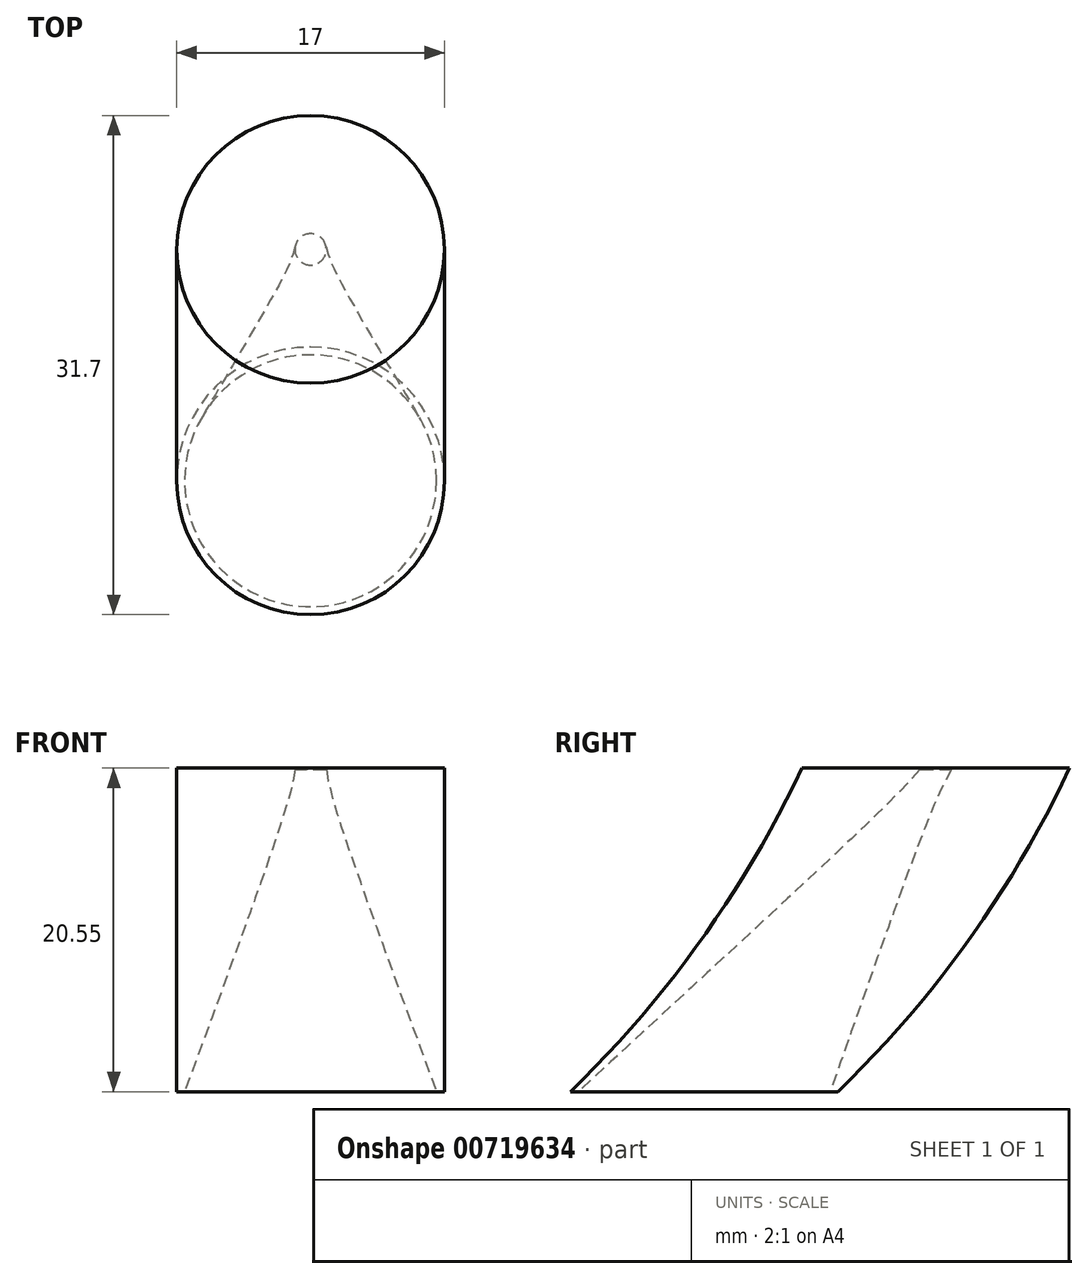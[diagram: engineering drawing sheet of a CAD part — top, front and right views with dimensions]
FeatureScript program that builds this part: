
annotation { "Feature Type Name" : "Feature", "Feature Type Description" : "" }
export const myFeature = defineFeature(function(context is Context, id is Id, definition is map)
    precondition{}
    {
        {
            var Q0;
            Q0=qCreatedBy(makeId("Top.planeOp"),FACE);
            var sketch = newSketch(context, id + "F0", { "sketchPlane" : qUnion([Q0])});
            skCircle(sketch, "E0", {"center": v(0, 0) * mm, "radius": 8.5 * mm});
            skSolve(sketch);
        }
        {
            var Q0;
            Q0=qCreatedBy(makeId("Right.planeOp"),FACE);
            var sketch = newSketch(context, id + "F1", { "sketchPlane" : qUnion([Q0])});
            skArc(sketch, "E1", {"start": v(0, 0) * mm, "mid": v(8.29, 9.6) * mm, "end": v(14.7, 20.55) * mm});
            skSolve(sketch);
        }
        {
            var Q0;
            Q0=qSketchRegion(id+"F0",true);
            var Q1;
            Q1=qConstructionFilter(qBodyType(qCreatedBy(id+"F1",EDGE),BodyType.WIRE),ConstructionObject.NO);
            sweep(context, id + "F2", {"profiles" : qUnion([Q0]), "path" : qUnion([Q1]), "keepProfileOrientation" : true});
        }
        {
            var Q0;
            Q0=makeQuery(id+"F2.opSweep","CAP_FACE",FACE,{"disambiguationData":[OSD([sQuery(id+"F0.wireOp",EDGE,"E0"),sQuery(id+"F1.wireOp",VERTEX,"E1.end")])],"isStart":false});
            var sketch = newSketch(context, id + "F3", { "sketchPlane" : qUnion([Q0])});
            skCircle(sketch, "E2", {"center": v(0, 14.7) * mm, "radius": 8 * mm});
            skSolve(sketch);
        }
        {
            var Q0;
            Q0=qCreatedBy(makeId("Top.planeOp"),FACE);
            var sketch = newSketch(context, id + "F4", { "sketchPlane" : qUnion([Q0])});
            skCircle(sketch, "E3", {"center": v(0, 0) * mm, "radius": 8 * mm});
            skSolve(sketch);
        }
        {
            var Q0;
            Q0=makeQuery(id+"F3.imprint","IMPRINT",FACE,{"disambiguationData":[TD([[makeQuery(id+"F3.imprint","IMPRINT",EDGE,{"derivedFrom":sQuery(id+"F3.wireOp",EDGE,"E2")}),1.0]])]});
            cPlane(context, id + "F5", {"entities" : qUnion([Q0]), "cplaneType" : CPlaneType.OFFSET, "offset" : 0.1 * mm, "oppositeDirection" : true, "width" : 150 * mm, "height" : 150 * mm});
        }
        {
            var Q0;
            Q0=qCreatedBy(id+"F5.planeOp",FACE);
            var sketch = newSketch(context, id + "F6", { "sketchPlane" : qUnion([Q0])});
            skCircle(sketch, "E4", {"center": v(0, 14.7) * mm, "radius": 1 * mm});
            skSolve(sketch);
        }
        {
            var Q1;
            Q1=qSketchRegion(id+"F4",true);
            var Q2;
            Q2=qSketchRegion(id+"F6",true);
            loft(context, id + "F7", {"operationType" : NewBodyOperationType.REMOVE, "sheetProfilesArray" : [{ "sheetProfileEntities" : qUnion([Q1]) }, { "sheetProfileEntities" : qUnion([Q2]) }]});
        }
    });
